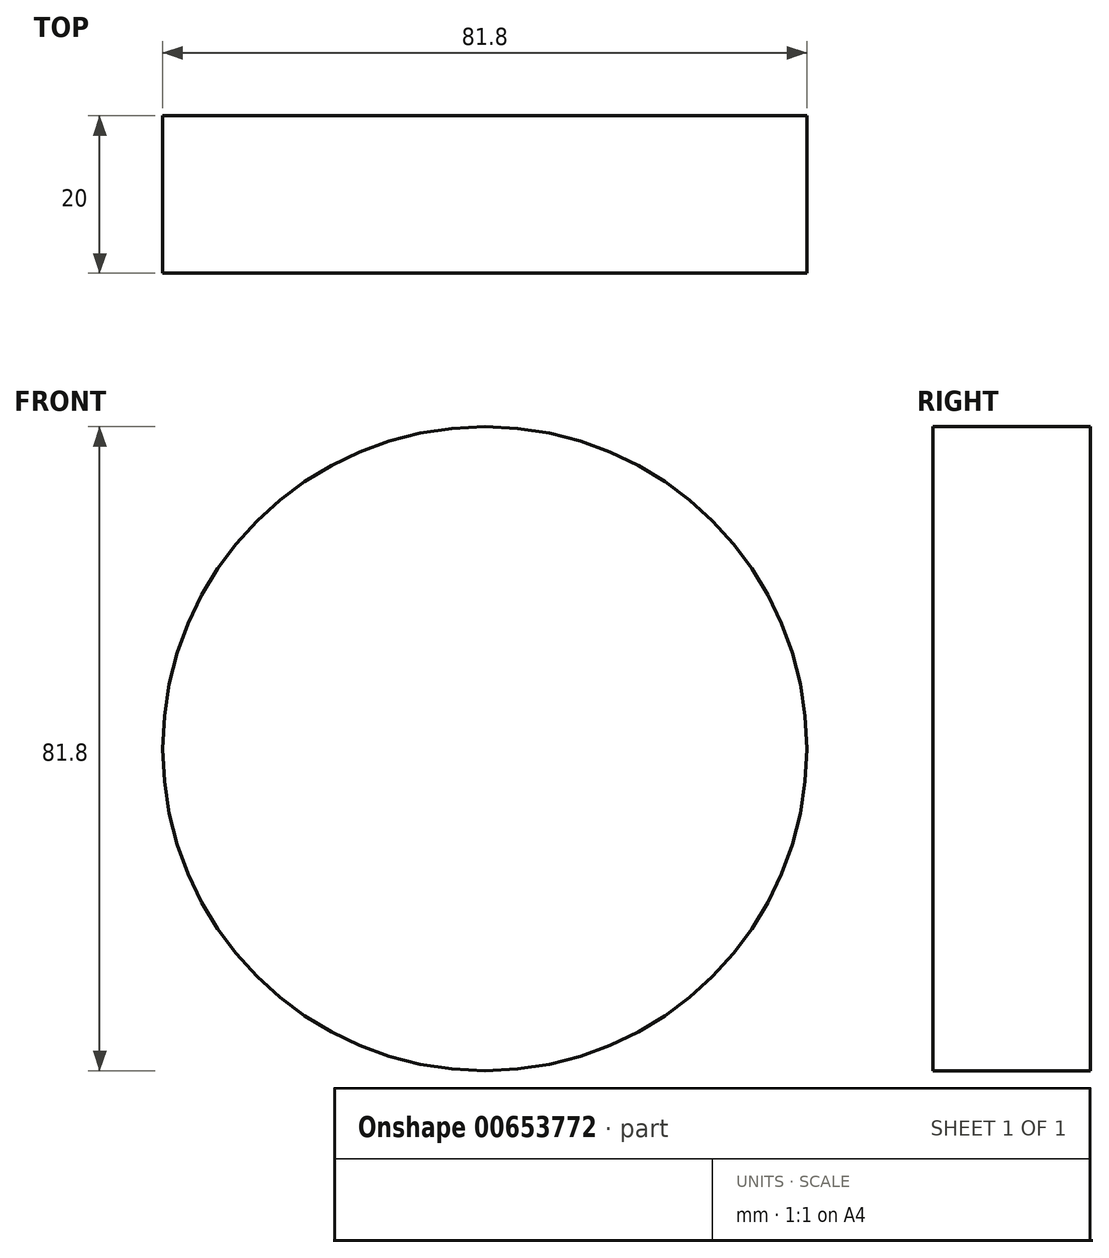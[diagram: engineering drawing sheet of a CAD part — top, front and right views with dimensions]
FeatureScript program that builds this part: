
annotation { "Feature Type Name" : "Feature", "Feature Type Description" : "" }
export const myFeature = defineFeature(function(context is Context, id is Id, definition is map)
    precondition{}
    {
        {
            var Q0;
            Q0=qCreatedBy(makeId("Front.planeOp"),FACE);
            var sketch = newSketch(context, id + "F0", { "sketchPlane" : qUnion([Q0])});
            skCircle(sketch, "E0", {"center": v(0, 0) * mm, "radius": 40.9 * mm});
            skSolve(sketch);
        }
        {
            var Q0;
            Q0=makeQuery(id+"F0.imprint","IMPRINT",FACE,{"disambiguationData":[TD([[makeQuery(id+"F0.imprint","IMPRINT",EDGE,{"derivedFrom":sQuery(id+"F0.wireOp",EDGE,"E0")}),1.0]])]});
            extrude(context, id + "F1", {"entities" : qUnion([Q0]), "depth" : 20 * mm, "offsetDistance" : 25 * mm});
        }
    });
